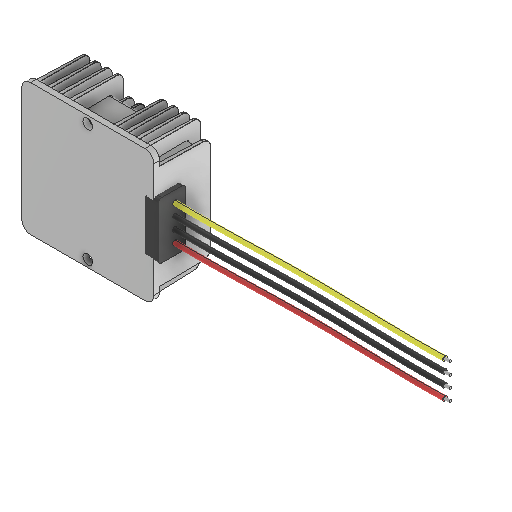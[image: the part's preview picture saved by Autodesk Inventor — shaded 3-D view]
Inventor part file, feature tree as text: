
AUTODESK INVENTOR PART (.ipt)
format: ipt  version: 2024.1 (Build 281209000, 209)  size: 650,752 bytes
history: native  units: mm
features: fillet x1, other x1
ambient origin geometry x8: Origin, YZ Plane, XZ Plane, XY Plane, X Axis, Y Axis, Z Axis, Center Point
bodies: Volumenkörper1 (feature_tree), Volumenkörper2 (feature_tree)
feature tree (2):
  fillet  "Fillet3"  [1 undecoded]
  other  "Boss-Extrude10"
note: 1 required parameter value undecoded (feature->parameter linkage not recoverable at this tier; creation-order binding heuristic only, values carry confidence <= 0.55)
